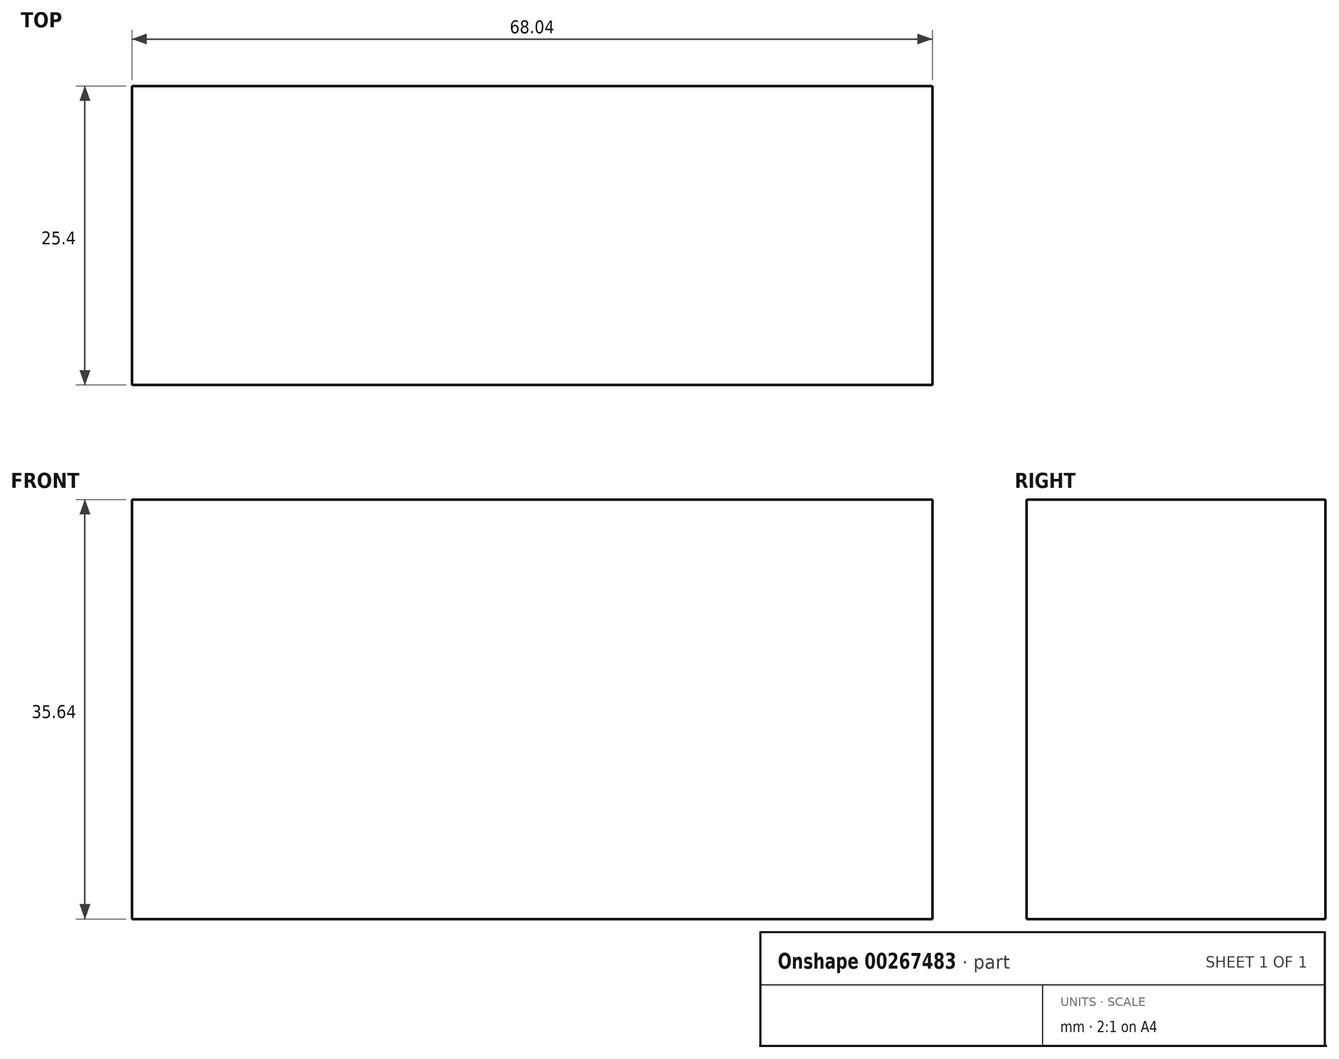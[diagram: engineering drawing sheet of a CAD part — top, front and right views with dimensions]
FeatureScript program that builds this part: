
annotation { "Feature Type Name" : "Feature", "Feature Type Description" : "" }
export const myFeature = defineFeature(function(context is Context, id is Id, definition is map)
    precondition{}
    {
        {
            var Q0;
            Q0=qCreatedBy(makeId("Front.planeOp"),FACE);
            var sketch = newSketch(context, id + "F0", { "sketchPlane" : qUnion([Q0])});
            skLineSegment(sketch, "E0.bottom", {"start": v(-38.23, 45.85) * mm, "end": v(29.81, 45.85) * mm});
            skLineSegment(sketch, "E0.top", {"start": v(-38.23, 10.2) * mm, "end": v(29.81, 10.2) * mm});
            skLineSegment(sketch, "E0.left", {"start": v(-38.23, 45.85) * mm, "end": v(-38.23, 10.2) * mm});
            skLineSegment(sketch, "E0.right", {"start": v(29.81, 45.85) * mm, "end": v(29.81, 10.2) * mm});
            skSolve(sketch);
        }
        {
            var Q0;
            Q0 = qSketchRegion(id + "F0", true);
            extrude(context, id + "F1", {"entities" : qUnion([Q0]), "depth" : 25.4 * mm});
        }
    });
